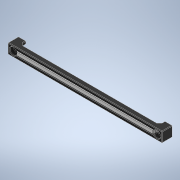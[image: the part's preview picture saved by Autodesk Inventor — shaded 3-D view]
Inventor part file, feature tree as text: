
AUTODESK INVENTOR PART (.ipt)
format: ipt  version: 2021 (Build 250183000, 183)  size: 794,112 bytes
history: native  units: mm
features: extrude x14, sketch x14, chamfer x10, thicken_offset x5, fillet x4, plane x3, mirror x3, projected_geometry x3
ambient origin geometry x8: Origin, YZ Plane, XZ Plane, XY Plane, X Axis, Y Axis, Z Axis, Center Point
bodies: Solid1 (feature_tree), Solid2 (feature_tree)
feature tree (56):
  extrude  "Extrusion1"  Depth=10.0mm
  extrude  "Extrusion2"  Depth=10.0mm
  extrude  "Extrusion3"  Depth=5.0mm
  sketch  "Sketch4"  dims[d10=0.0mm d11=0.0mm d12=1.6mm]
  plane  "Work Plane1"
  extrude  "Extrusion5"  Depth=1.6mm
  extrude  "Extrusion6"  Depth=5.6mm
  sketch  "Sketch6"  dims[d21=2.0mm d22=3.75mm d23=0.0mm d25=5.3mm d27=0.0mm d28=0.0mm]
  plane  "Work Plane2"
  extrude  "Extrusion7"  Depth=5.3mm
  mirror  "Mirror1"
  chamfer  "Chamfer3"  [1 undecoded]
  chamfer  "Chamfer5"  Distance=3.75mm
  chamfer  "Chamfer6"  Distance=0.5mm Angle=45.0deg
  extrude  "Extrusion8"  Depth=70.0mm
  chamfer  "Chamfer7"  Distance=1.9mm Angle=45.0deg
  chamfer  "Chamfer8"  [1 undecoded]
  thicken_offset  "Thicken1"
  thicken_offset  "Thicken2"
  chamfer  "Chamfer9"  Distance=0.5mm Angle=45.0deg
  extrude  "Extrusion9"  Depth=0.2mm
  chamfer  "Chamfer11"  Distance=0.2mm
  extrude  "Extrusion10"  Depth=1.5mm
  extrude  "Extrusion11"  Depth=1.5mm TaperAngle=45.0deg
  mirror  "Mirror2"
  extrude  "Extrusion12"  Depth=1.5mm
  sketch  "Sketch13"  dims[d45=0.5mm d46=2.0mm d47=45.0deg d48=70.0mm d49=1.9mm d50=2.0mm d51=45.0deg d52=0.0mm d53=0.0mm d54=0.5mm d55=2.0mm d56=45.0deg]
  mirror  "Mirror3"
  extrude  "Extrusion13"  Depth=1.5mm
  extrude  "Extrusion14"  Depth=5.0mm
  fillet  "Fillet2"  Radius=2.5mm
  chamfer  "Chamfer14"  Distance=0.5mm Angle=45.0deg
  chamfer  "Chamfer15"  [1 undecoded]
  fillet  "Fillet4"  Radius=10.0mm
  thicken_offset  "Thicken3"
  fillet  "Fillet5"  Radius=3.0mm
  thicken_offset  "Thicken4"
  thicken_offset  "Thicken5"
  fillet  "Fillet6"  [1 undecoded]
  extrude  "Extrusion15"  Depth=1.5mm
  chamfer  "Chamfer16"  Distance=3.0mm
  sketch  "Sketch1"  dims[d0=150.0mm d1=10.0mm]
  sketch  "Sketch2"  dims[d2=10.0mm d3=0.0mm d7=67.5mm]
  sketch  "Sketch3"  dims[d8=135.0mm d9=5.0mm]
  sketch  "Sketch5"  dims[d13=2.0mm d14=0.0mm d18=5.6mm]
  projected_geometry  "Projected Loop1"
  plane  "Work Plane3"
  sketch  "Sketch7"  dims[d29=-2.0mm d30=3.75mm d31=0.0mm]
  sketch  "Sketch8"  dims[d32=2.0mm]
  sketch  "Sketch9"  dims[d33=3.0mm]
  sketch  "Sketch10"  dims[d34=2.8mm]
  projected_geometry  "Projected Loop2"
  projected_geometry  "Projected Loop3"
  sketch  "Sketch12"  dims[d35=5.6mm d39=0.5mm d40=2.0mm d41=45.0deg]
  sketch  "Sketch14"  dims[d57=0.5mm d58=2.0mm d59=45.0deg d60=0.2mm]
  sketch  "Sketch18"  dims[d61=0.2mm d62=0.2mm d63=0.2mm d64=0.5mm d65=2.0mm d66=45.0deg d70=6.5mm d71=3.0mm d72=5.0mm d73=2.5mm d74=0.0mm d75=0.5mm d76=2.0mm d77=45.0deg d78=0.0mm d79=0.0mm d80=10.0mm d81=0.0mm d88=3.0mm d89=0.0mm d90=0.0mm d91=0.0mm d93=0.56mm d94=3.0mm d95=0.0mm d96=1.5mm d97=0.5mm d98=2.0mm d99=45.0deg d101=0.5mm d102=2.0mm d103=45.0deg d104=1.5mm d105=0.25mm d106=0.25mm d107=0.5mm d108=2.116859mm d109=0.25mm d110=0.25mm d111=0.25mm d112=0.25mm d113=1.5mm d114=3.1mm d115=0.35mm d116=1.55mm d117=3.0mm d118=0.0mm d119=0.5mm d120=2.0mm d121=45.0deg]
note: 4 required parameter values undecoded (feature->parameter linkage not recoverable at this tier; creation-order binding heuristic only, values carry confidence <= 0.55)
